# Revit family: Faucet-Lavatory-KALLISTA-Grid-P26100
name_source: partatom
category: Plumbing Fixtures
units: mm (PartAtom-declared; Revit-internal decimal feet)

## family parameters
Cut with Voids When Loaded = No
Host = Face
Maintain Annotation Orientation = No
OmniClass Number = 23.31.11.00
OmniClass Title = Faucets
Part Type = Normal
Room Calculation Point = No
Round Connector Dimension = Use Diameter
Shared = No

## types (1)
- BL-Matte Black
    ADA Compliant = Yes
    Assembly Code = D2010
    CW Connection = Yes
    Cold Water Inlet = Cold Water Inlet
    Date Modified = 05/20/2025
    Default Elevation = 36"
    Description = Sink Faucet, Cube Handles
    Drain Included = Yes
    Finish = Kallista-Metal-BL-Matte_Black
    Flow Rate = 1 GPM
    HW Connection = Yes
    Handle Clearance = 1 15/16"
    Height = 5 5/16"
    Hot Water Inlet = Hot Water Inlet
    Length = 5 1/16"
    Manufacturer = Kallista Co.
    Master Format 2014 = 22 41 39
    Master Format 2014 Name = Residential Faucets, Supplies, and Trim
    Material = Premium Metal Construction
    Model = P26100-CU-BL
    Pressure = 0.00 psi
    Product Documentation Link = https://techcomm.kohler.com
    Product Name = Grid
    Product Page URL = https://www.kallista.com
    Spout Reach = 5 1/16"
    Type = 1
    URL = https://www.kallista.com
    Vent Connection = No
    Waste Connection = No
    Waste Water Outlet = Waste Water Outlet
    WaterSense Certified = No

## geometry (parser evidence)
native form markers: Sweep x8
no freeform markers — native parametric forms only
